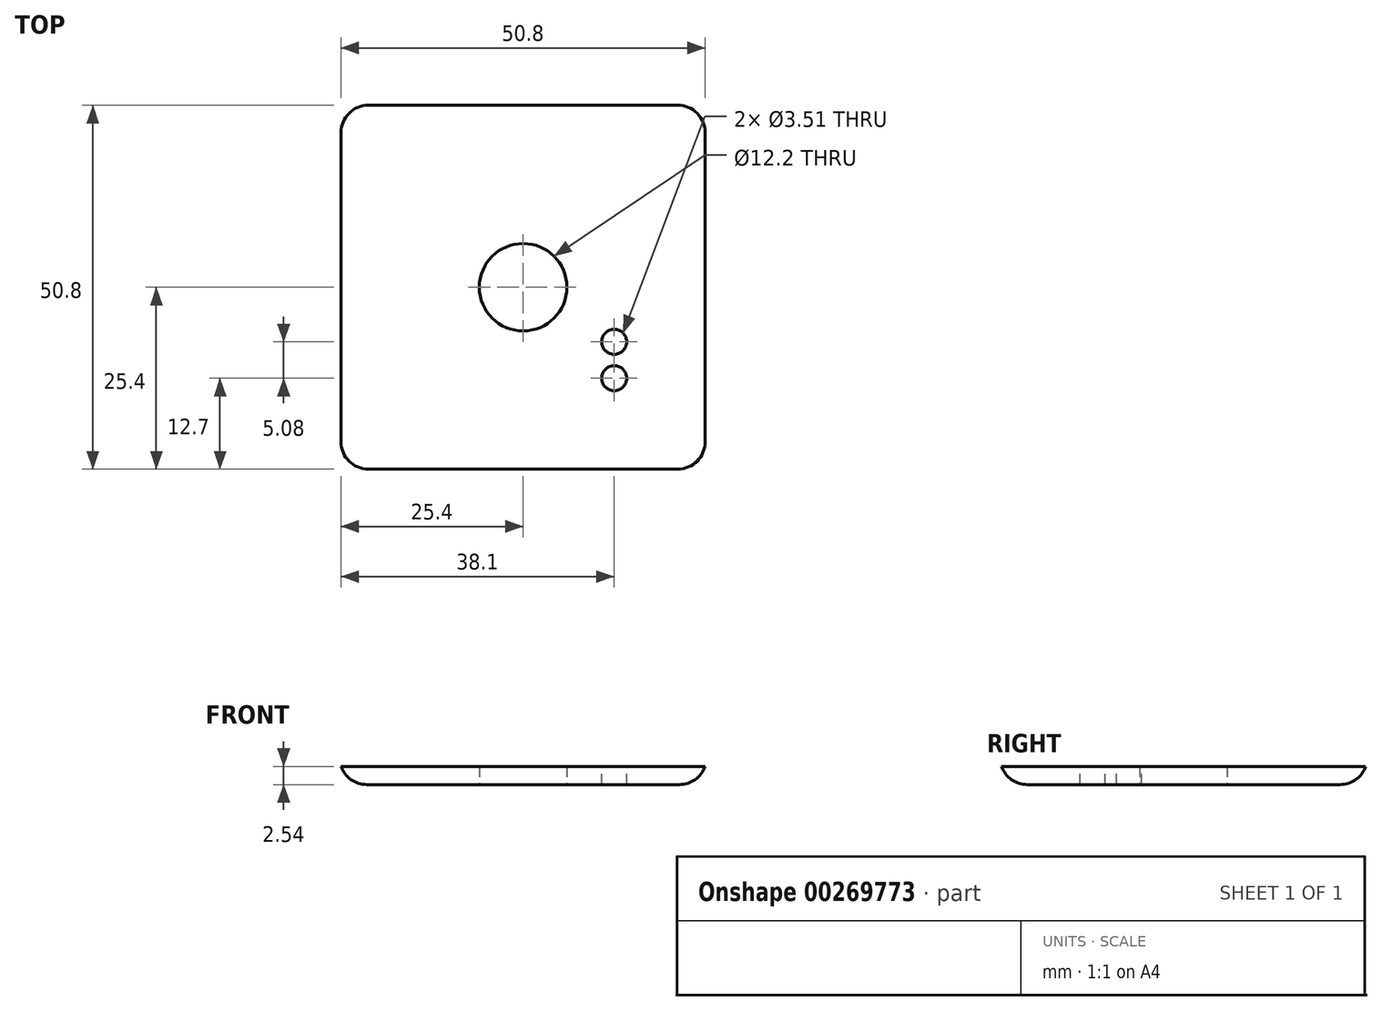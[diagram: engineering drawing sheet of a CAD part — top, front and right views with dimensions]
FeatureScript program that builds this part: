
annotation { "Feature Type Name" : "Feature", "Feature Type Description" : "" }
export const myFeature = defineFeature(function(context is Context, id is Id, definition is map)
    precondition{}
    {
        {
            var Q0;
            Q0=qCreatedBy(makeId("Top.planeOp"),FACE);
            var sketch = newSketch(context, id + "F0", { "sketchPlane" : qUnion([Q0])});
            skLineSegment(sketch, "E0.bottom", {"start": v(3.81, 0) * mm, "end": v(47, 0) * mm});
            skLineSegment(sketch, "E0.top", {"start": v(3.8, 50.8) * mm, "end": v(47, 50.8) * mm});
            skLineSegment(sketch, "E0.left", {"start": v(0, 3.81) * mm, "end": v(0, 46.99) * mm});
            skLineSegment(sketch, "E0.right", {"start": v(50.8, 3.81) * mm, "end": v(50.8, 46.99) * mm});
            skPoint(sketch, "E1.visualSharp", {"position": v(0, 50.8) * mm});
            skArc(sketch, "E1.filletArc", {"start": v(3.8, 50.8) * mm, "mid": v(1.12, 49.68) * mm, "end": v(0, 46.99) * mm});
            skPoint(sketch, "E2.visualSharp", {"position": v(50.8, 50.8) * mm});
            skArc(sketch, "E2.filletArc", {"start": v(50.8, 46.99) * mm, "mid": v(49.68, 49.68) * mm, "end": v(47, 50.8) * mm});
            skPoint(sketch, "E3.visualSharp", {"position": v(50.8, 0) * mm});
            skArc(sketch, "E3.filletArc", {"start": v(47, 0) * mm, "mid": v(49.68, 1.12) * mm, "end": v(50.8, 3.81) * mm});
            skPoint(sketch, "E4.visualSharp", {"position": v(0, 0) * mm});
            skArc(sketch, "E4.filletArc", {"start": v(0, 3.8) * mm, "mid": v(1.12, 1.12) * mm, "end": v(3.81, 0) * mm});
            skLineSegment(sketch, "E5", {"start": v(25.4, 0) * mm, "end": v(25.4, 50.8) * mm, "construction": true});
            skCircle(sketch, "E6", {"center": v(12.7, 12.7) * mm, "radius": 1.75 * mm});
            skCircle(sketch, "E7", {"center": v(12.7, 17.78) * mm, "radius": 1.75 * mm});
            skCircle(sketch, "E8.MirrorC", {"center": v(38.1, 17.78) * mm, "radius": 1.75 * mm});
            skCircle(sketch, "E9.MirrorC", {"center": v(38.1, 12.7) * mm, "radius": 1.75 * mm});
            skSolve(sketch);
        }
        {
            var Q0;
            Q0 = qSketchRegion(id + "F0", true);
            var Q1;
            Q1=makeQuery(id+"F0.imprint","IMPRINT",FACE,{"disambiguationData":[TD([[makeQuery(id+"F0.imprint","IMPRINT",EDGE,{"derivedFrom":sQuery(id+"F0.wireOp",EDGE,"E7")}),1.0]])]});
            var Q2;
            Q2=makeQuery(id+"F0.imprint","IMPRINT",FACE,{"disambiguationData":[TD([[makeQuery(id+"F0.imprint","IMPRINT",EDGE,{"derivedFrom":sQuery(id+"F0.wireOp",EDGE,"E8.MirrorC")}),-1.0]])]});
            var Q3;
            Q3=makeQuery(id+"F0.imprint","IMPRINT",FACE,{"disambiguationData":[TD([[makeQuery(id+"F0.imprint","IMPRINT",EDGE,{"derivedFrom":sQuery(id+"F0.wireOp",EDGE,"E6")}),1.0]])]});
            var Q4;
            Q4=makeQuery(id+"F0.imprint","IMPRINT",FACE,{"disambiguationData":[TD([[makeQuery(id+"F0.imprint","IMPRINT",EDGE,{"derivedFrom":sQuery(id+"F0.wireOp",EDGE,"E9.MirrorC")}),-1.0]])]});
            extrude(context, id + "F1", {"entities" : qUnion([Q0, Q1, Q2, Q3, Q4]), "oppositeDirection" : true, "depth" : 10.16 * mm});
        }
        {
            var Q0;
            Q0=makeQuery(id+"F0.imprint","IMPRINT",FACE,{"disambiguationData":[TD([[makeQuery(id+"F0.imprint","IMPRINT",EDGE,{"derivedFrom":sQuery(id+"F0.wireOp",EDGE,"E7")}),1.0]])]});
            var Q1;
            Q1=makeQuery(id+"F0.imprint","IMPRINT",FACE,{"disambiguationData":[TD([[makeQuery(id+"F0.imprint","IMPRINT",EDGE,{"derivedFrom":sQuery(id+"F0.wireOp",EDGE,"E8.MirrorC")}),-1.0]])]});
            var Q2;
            Q2=makeQuery(id+"F0.imprint","IMPRINT",FACE,{"disambiguationData":[TD([[makeQuery(id+"F0.imprint","IMPRINT",EDGE,{"derivedFrom":sQuery(id+"F0.wireOp",EDGE,"E9.MirrorC")}),-1.0]])]});
            var Q3;
            Q3=makeQuery(id+"F0.imprint","IMPRINT",FACE,{"disambiguationData":[TD([[makeQuery(id+"F0.imprint","IMPRINT",EDGE,{"derivedFrom":sQuery(id+"F0.wireOp",EDGE,"E6")}),1.0]])]});
            extrude(context, id + "F2", {"entities" : qUnion([Q0, Q1, Q2, Q3]), "operationType" : NewBodyOperationType.REMOVE, "oppositeDirection" : true, "depth" : 7.62 * mm});
        }
        {
            var Q0;
            Q0=makeQuery(id+"F1.opExtrude","CAP_FACE",FACE,{"disambiguationData":[OSD([sQuery(id+"F0.wireOp",EDGE,"E0.bottom"),sQuery(id+"F0.wireOp",EDGE,"E0.top"),sQuery(id+"F0.wireOp",EDGE,"E0.left"),sQuery(id+"F0.wireOp",EDGE,"E0.right"),sQuery(id+"F0.wireOp",EDGE,"E1.filletArc"),sQuery(id+"F0.wireOp",EDGE,"E2.filletArc"),sQuery(id+"F0.wireOp",EDGE,"E3.filletArc"),sQuery(id+"F0.wireOp",EDGE,"E4.filletArc")])],"isStart":false});
            var sketch = newSketch(context, id + "F3", { "sketchPlane" : qUnion([Q0])});
            skCircle(sketch, "E10", {"center": v(25.4, -25.4) * mm, "radius": 6.1 * mm});
            skPoint(sketch, "E10.centerSnap0", {"position": v(50.8, -25.4) * mm});
            skPoint(sketch, "E10.centerSnap1", {"position": v(25.4, 0) * mm});
            skSolve(sketch);
        }
        {
            var Q0;
            Q0 = qSketchRegion(id + "F3", true);
            extrude(context, id + "F4", {"entities" : qUnion([Q0]), "operationType" : NewBodyOperationType.REMOVE, "oppositeDirection" : true, "depth" : 3.2 * mm});
        }
        {
            var Q0;
            Q0=makeQuery(id+"F1.opExtrude","CAP_EDGE",EDGE,{"disambiguationData":[OSD([sQuery(id+"F0.wireOp",EDGE,"E0.bottom")])],"isStart":false});
            fillet(context, id + "F5", {"entities" : qUnion([Q0]), "radius" : 3.8 * mm, "tangentPropagation" : true, "allowEdgeOverflow" : false});
        }
    });
